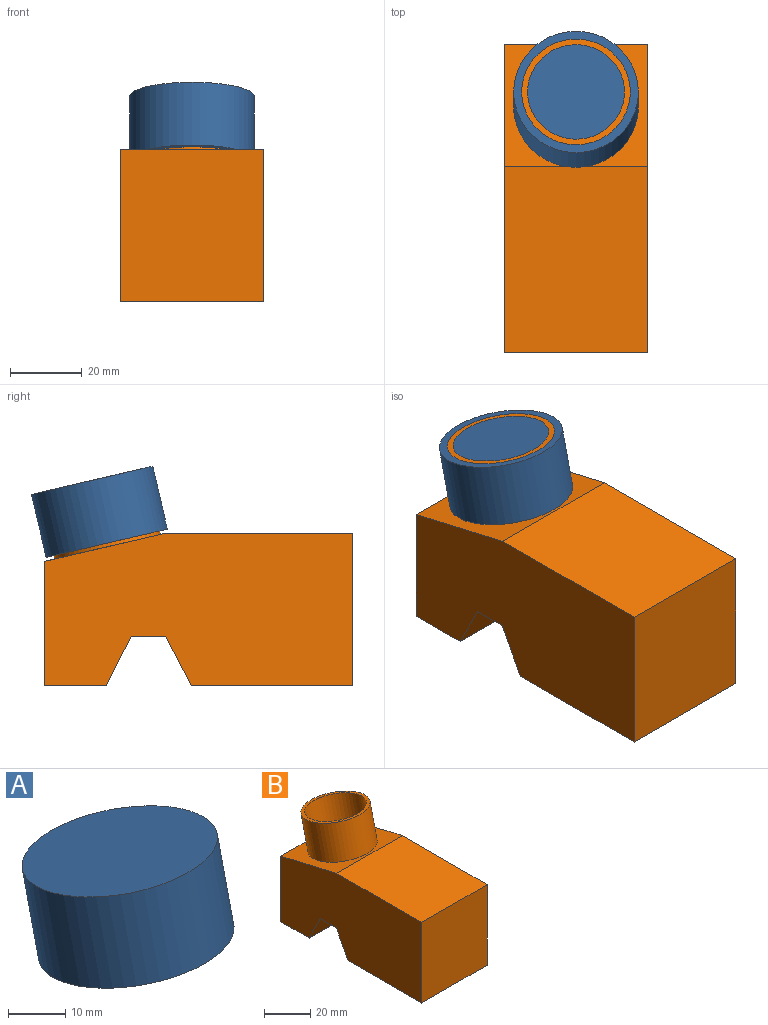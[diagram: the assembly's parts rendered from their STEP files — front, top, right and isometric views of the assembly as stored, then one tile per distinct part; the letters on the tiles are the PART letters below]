
ASSEMBLY  parts=2 mates=1
PART A: 5 faces, bbox 34.7x37.9x25.4 mm
  f0: cylinder r=17.37mm len=37.91mm, axis (0,-0.23,-0.97), area 1964.5mm2, adj f1,f2
  f1: plane 34.74x33.84mm, normal (0,0.23,0.97), area 947.8mm2, adj f0
  f2: plane 34.74x33.84mm, normal (0,-0.23,-0.97), area 217.5mm2, adj f0,f3
  f3: cylinder r=15.25mm len=33.55mm, axis (0,-0.23,-0.97), area 1628.6mm2, adj f2,f4
  f4: plane 30.49x29.7mm, normal (0,-0.23,-0.97), area 730.4mm2, adj f3
PART B: 15 faces, bbox 40x87.3x60.7 mm
  f0: plane 51.86x40mm, normal (0,0,1), area 2074.4mm2, adj f1,f8,f9,f10
  f1: plane 42.58x40mm, normal (0,-1,0), area 1703.1mm2, adj f0,f2,f9,f10
  f2: plane 44.9x40mm, normal (0,0,-1), area 1795.9mm2, adj f1,f3,f9,f10
  f3: plane 40x13.69mm, normal (0,0.88,-0.47), area 618.6mm2, adj f2,f4,f9,f10
  f4: plane 40x9.6mm, normal (0,0,-1), area 384.1mm2, adj f3,f5,f9,f10
  f5: plane 40x13.69mm, normal (0,-0.89,-0.45), area 614.2mm2, adj f4,f6,f9,f10
  f6: plane 40x17.29mm, normal (0,0,-1), area 691.5mm2, adj f5,f7,f9,f10
  f7: plane 40x34.66mm, normal (0,1,0), area 1386.2mm2, adj f6,f8,f9,f10
  f8: plane 40x34.09mm, normal (0,0.23,0.97), area 680.5mm2, adj f0,f7,f9,f10,f12
  f9: plane 85.95x42.58mm, normal (1,0,0), area 3296.3mm2, adj f0,f1,f2,f3,f4,f5,f6,f7
  f10: plane 85.95x42.58mm, normal (-1,0,0), area 3296.3mm2, adj f0,f1,f2,f3,f4,f5,f6,f7
  f11: cylinder r=13.52mm len=30.65mm, axis (0,-0.23,-0.97), area 1614.5mm2, adj f13,f14
  f12: cylinder r=15.13mm len=33.78mm, axis (0,-0.23,-0.97), area 1806.7mm2, adj f8,f13
  f13: plane 30.27x29.48mm, normal (0,0.23,0.97), area 145mm2, adj f11,f12
  f14: plane 27.05x26.35mm, normal (0,0.23,0.97), area 574.6mm2, adj f11
PLACE A rot(axis=(0,-0.23,-0.97),90deg) t=(-55.71,-54.37,4.32)mm
PLACE B t=(-16.34,-0.95,10.38)mm
MATE slider A.f3 <-> B.f11  axis (0,0.23,0.97) through (-16.34,8.01,48.92)mm
